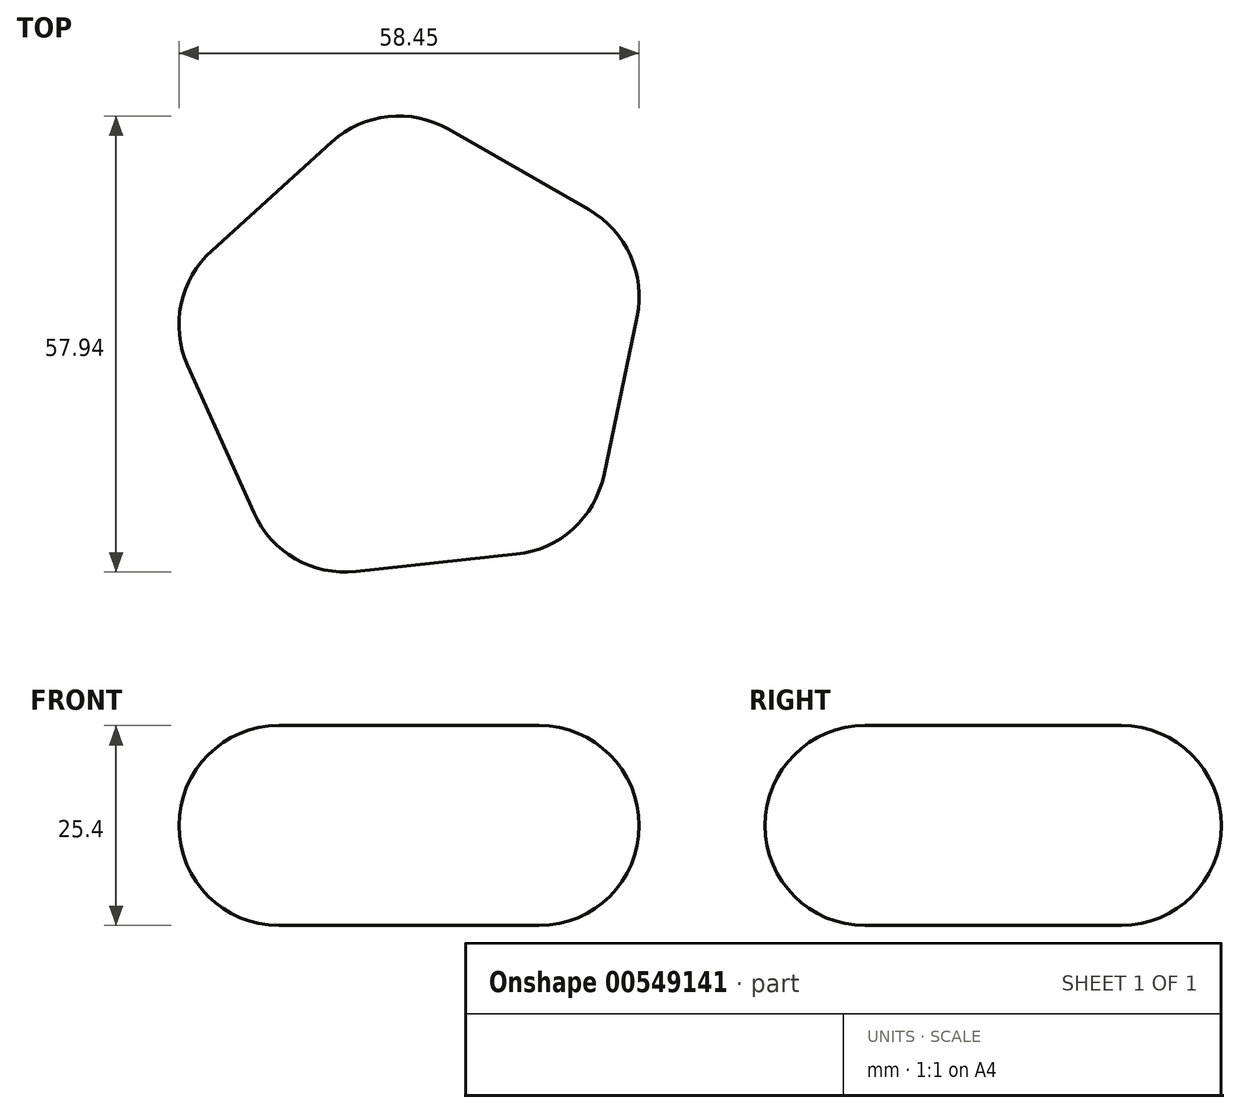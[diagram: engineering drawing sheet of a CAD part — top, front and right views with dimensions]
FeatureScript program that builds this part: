
annotation { "Feature Type Name" : "Feature", "Feature Type Description" : "" }
export const myFeature = defineFeature(function(context is Context, id is Id, definition is map)
    precondition{}
    {
        {
            var Q0;
            Q0=qCreatedBy(makeId("Top.planeOp"),FACE);
            var sketch = newSketch(context, id + "F0", { "sketchPlane" : qUnion([Q0])});
            skCircle(sketch, "E0.cCircle", {"center": v(0, 0) * mm, "radius": 26.84 * mm, "construction": true});
            skLineSegment(sketch, "E0.0", {"start": v(-3.56, 32.98) * mm, "end": v(30.27, 13.58) * mm});
            skLineSegment(sketch, "E0.1", {"start": v(30.27, 13.58) * mm, "end": v(22.27, -24.6) * mm});
            skLineSegment(sketch, "E0.2", {"start": v(22.27, -24.6) * mm, "end": v(-16.5, -28.78) * mm});
            skLineSegment(sketch, "E0.3", {"start": v(-16.5, -28.78) * mm, "end": v(-32.47, 6.8) * mm});
            skLineSegment(sketch, "E0.4", {"start": v(-32.47, 6.8) * mm, "end": v(-3.56, 32.98) * mm});
            skPoint(sketch, "E0.0.midPoint", {"position": v(13.36, 23.28) * mm});
            skSolve(sketch);
        }
        {
            var Q0;
            Q0 = qSketchRegion(id + "F0", true);
            extrude(context, id + "F1", {"entities" : qUnion([Q0]), "depth" : 25.4 * mm, "offsetDistance" : 25.4 * mm});
        }
        {
            var Q0;
            Q0=makeQuery(id+"F1.opExtrude","SWEPT_FACE",FACE,{"disambiguationData":[OSD([sQuery(id+"F0.wireOp",EDGE,"E0.2")])]});
            var Q1;
            Q1=makeQuery(id+"F1.opExtrude","SWEPT_FACE",FACE,{"disambiguationData":[OSD([sQuery(id+"F0.wireOp",EDGE,"E0.3")])]});
            var Q2;
            Q2=makeQuery(id+"F1.opExtrude","SWEPT_FACE",FACE,{"disambiguationData":[OSD([sQuery(id+"F0.wireOp",EDGE,"E0.4")])]});
            var Q3;
            Q3=makeQuery(id+"F1.opExtrude","SWEPT_FACE",FACE,{"disambiguationData":[OSD([sQuery(id+"F0.wireOp",EDGE,"E0.0")])]});
            var Q4;
            Q4=makeQuery(id+"F1.opExtrude","SWEPT_FACE",FACE,{"disambiguationData":[OSD([sQuery(id+"F0.wireOp",EDGE,"E0.1")])]});
            var Q5;
            Q5=makeQuery(id+"F1.opExtrude","CAP_EDGE",EDGE,{"disambiguationData":[OSD([sQuery(id+"F0.wireOp",EDGE,"E0.1")])],"isStart":false});
            var Q6;
            Q6=makeQuery(id+"F1.opExtrude","CAP_FACE",FACE,{"disambiguationData":[OSD([sQuery(id+"F0.wireOp",EDGE,"E0.0"),sQuery(id+"F0.wireOp",EDGE,"E0.1"),sQuery(id+"F0.wireOp",EDGE,"E0.2"),sQuery(id+"F0.wireOp",EDGE,"E0.3"),sQuery(id+"F0.wireOp",EDGE,"E0.4")])],"isStart":false});
            fillet(context, id + "F2", {"entities" : qUnion([Q0, Q1, Q2, Q3, Q4, Q5, Q6]), "tangentPropagation" : true, "radius" : 12.7 * mm, "defaultsChanged" : true, "vertexSettings" : [], "allowEdgeOverflow" : false});
        }
    });
